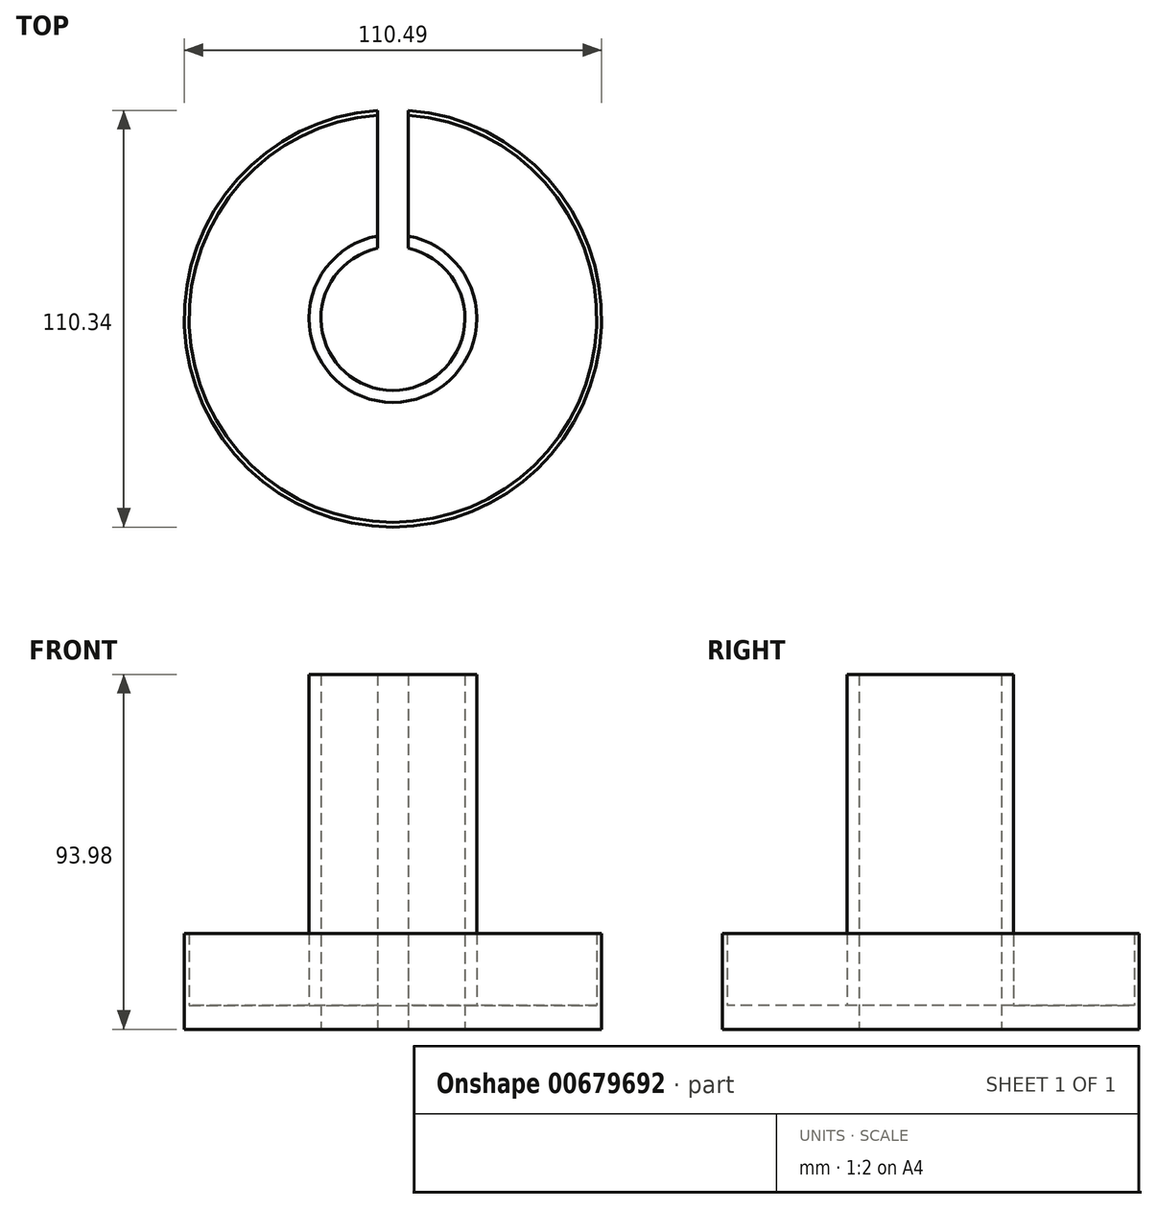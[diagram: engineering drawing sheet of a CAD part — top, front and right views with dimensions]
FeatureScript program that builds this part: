
annotation { "Feature Type Name" : "Feature", "Feature Type Description" : "" }
export const myFeature = defineFeature(function(context is Context, id is Id, definition is map)
    precondition{}
    {
        {
            var Q0;
            Q0=qCreatedBy(makeId("Top.planeOp"),FACE);
            var sketch = newSketch(context, id + "F0", { "sketchPlane" : qUnion([Q0])});
            skCircle(sketch, "E0", {"center": v(-5.2, -18.58) * mm, "radius": 53.98 * mm});
            skCircle(sketch, "E1", {"center": v(-5.2, -18.58) * mm, "radius": 55.25 * mm});
            skCircle(sketch, "E2", {"center": v(-5.2, -18.58) * mm, "radius": 19.05 * mm});
            skCircle(sketch, "E3", {"center": v(-5.2, -18.58) * mm, "radius": 22.23 * mm});
            skLineSegment(sketch, "E4.bottom", {"start": v(-1.14, -67.48) * mm, "end": v(-9.26, -67.48) * mm});
            skLineSegment(sketch, "E4.top", {"start": v(-1.14, 140.81) * mm, "end": v(-9.26, 140.81) * mm});
            skLineSegment(sketch, "E4.left", {"start": v(-1.14, -67.48) * mm, "end": v(-1.14, 140.81) * mm});
            skLineSegment(sketch, "E4.right", {"start": v(-9.26, -67.48) * mm, "end": v(-9.26, 140.81) * mm});
            skPoint(sketch, "E4.middle", {"position": v(-5.2, 36.67) * mm});
            skSolve(sketch);
        }
        {
            var Q0;
            {var subQ0=sQuery(id+"F0.wireOp",EDGE,"E4.left");var subQ1=sQuery(id+"F0.wireOp",EDGE,"E0");var subQ2=makeQuery(id+"F0.imprint","INTERSECT",VERTEX,{"derivedFrom":[subQ1,subQ0]});Q0=makeQuery(id+"F0.imprint","IMPRINT",FACE,{"disambiguationData":[TD([[makeQuery(id+"F0.imprint","IMPRINT",EDGE,{"disambiguationData":[TD([[subQ2,1.0]])],"derivedFrom":subQ1}),-1.0]])]});}
            extrude(context, id + "F1", {"entities" : qUnion([Q0]), "depth" : 25.4 * mm, "offsetDistance" : 25.4 * mm});
        }
        {
            var Q0;
            {var subQ0=sQuery(id+"F0.wireOp",EDGE,"E4.bottom");Q0=makeQuery(id+"F0.imprint","IMPRINT",FACE,{"disambiguationData":[TD([[makeQuery(id+"F0.imprint","IMPRINT",EDGE,{"derivedFrom":subQ0}),1.0]])]});}
            var Q1;
            {var subQ0=sQuery(id+"F0.wireOp",EDGE,"E4.left");var subQ1=sQuery(id+"F0.wireOp",EDGE,"E2");var subQ2=makeQuery(id+"F0.imprint","INTERSECT",VERTEX,{"disambiguationData":[OD(0.0)],"derivedFrom":[subQ1,subQ0]});Q1=makeQuery(id+"F0.imprint","IMPRINT",FACE,{"disambiguationData":[TD([[makeQuery(id+"F0.imprint","IMPRINT",EDGE,{"disambiguationData":[TD([[subQ2,1.0]])],"derivedFrom":subQ1}),-1.0]])]});}
            var Q2;
            {var subQ0=sQuery(id+"F0.wireOp",EDGE,"E4.right");var subQ1=sQuery(id+"F0.wireOp",EDGE,"E2");var subQ2=makeQuery(id+"F0.imprint","INTERSECT",VERTEX,{"disambiguationData":[OD(1.0)],"derivedFrom":[subQ1,subQ0]});Q2=makeQuery(id+"F0.imprint","IMPRINT",FACE,{"disambiguationData":[TD([[makeQuery(id+"F0.imprint","IMPRINT",EDGE,{"disambiguationData":[TD([[subQ2,-1.0]])],"derivedFrom":subQ1}),-1.0]])]});}
            var Q3;
            {var subQ0=sQuery(id+"F0.wireOp",EDGE,"E4.right");var subQ1=sQuery(id+"F0.wireOp",EDGE,"E2");var subQ2=makeQuery(id+"F0.imprint","INTERSECT",VERTEX,{"disambiguationData":[OD(0.0)],"derivedFrom":[subQ1,subQ0]});Q3=makeQuery(id+"F0.imprint","IMPRINT",FACE,{"disambiguationData":[TD([[makeQuery(id+"F0.imprint","IMPRINT",EDGE,{"disambiguationData":[TD([[subQ2,-1.0]])],"derivedFrom":subQ1}),-1.0]])]});}
            var Q4;
            {var subQ5=sQuery(id+"F0.wireOp",EDGE,"E4.bottom");Q4=makeQuery(id+"F0.imprint","IMPRINT",FACE,{"disambiguationData":[TD([[makeQuery(id+"F0.imprint","IMPRINT",EDGE,{"derivedFrom":subQ5}),-1.0]])]});}
            extrude(context, id + "F2", {"entities" : qUnion([Q0, Q1, Q2, Q3, Q4]), "operationType" : NewBodyOperationType.ADD, "depth" : 6.35 * mm, "offsetDistance" : 25.4 * mm});
        }
        {
            var Q0;
            {var subQ0=sQuery(id+"F0.wireOp",EDGE,"E4.left");var subQ1=sQuery(id+"F0.wireOp",EDGE,"E2");var subQ2=makeQuery(id+"F0.imprint","INTERSECT",VERTEX,{"disambiguationData":[OD(0.0)],"derivedFrom":[subQ1,subQ0]});Q0=makeQuery(id+"F0.imprint","IMPRINT",FACE,{"disambiguationData":[TD([[makeQuery(id+"F0.imprint","IMPRINT",EDGE,{"disambiguationData":[TD([[subQ2,1.0]])],"derivedFrom":subQ1}),-1.0]])]});}
            var Q1;
            {var subQ0=sQuery(id+"F0.wireOp",EDGE,"E4.right");var subQ1=sQuery(id+"F0.wireOp",EDGE,"E2");var subQ2=makeQuery(id+"F0.imprint","INTERSECT",VERTEX,{"disambiguationData":[OD(1.0)],"derivedFrom":[subQ1,subQ0]});Q1=makeQuery(id+"F0.imprint","IMPRINT",FACE,{"disambiguationData":[TD([[makeQuery(id+"F0.imprint","IMPRINT",EDGE,{"disambiguationData":[TD([[subQ2,-1.0]])],"derivedFrom":subQ1}),-1.0]])]});}
            var Q2;
            {var subQ0=sQuery(id+"F0.wireOp",EDGE,"E4.right");var subQ1=sQuery(id+"F0.wireOp",EDGE,"E2");var subQ2=makeQuery(id+"F0.imprint","INTERSECT",VERTEX,{"disambiguationData":[OD(0.0)],"derivedFrom":[subQ1,subQ0]});Q2=makeQuery(id+"F0.imprint","IMPRINT",FACE,{"disambiguationData":[TD([[makeQuery(id+"F0.imprint","IMPRINT",EDGE,{"disambiguationData":[TD([[subQ2,-1.0]])],"derivedFrom":subQ1}),-1.0]])]});}
            extrude(context, id + "F3", {"entities" : qUnion([Q0, Q1, Q2]), "operationType" : NewBodyOperationType.ADD, "depth" : 93.98 * mm, "offsetDistance" : 25.4 * mm});
        }
    });
